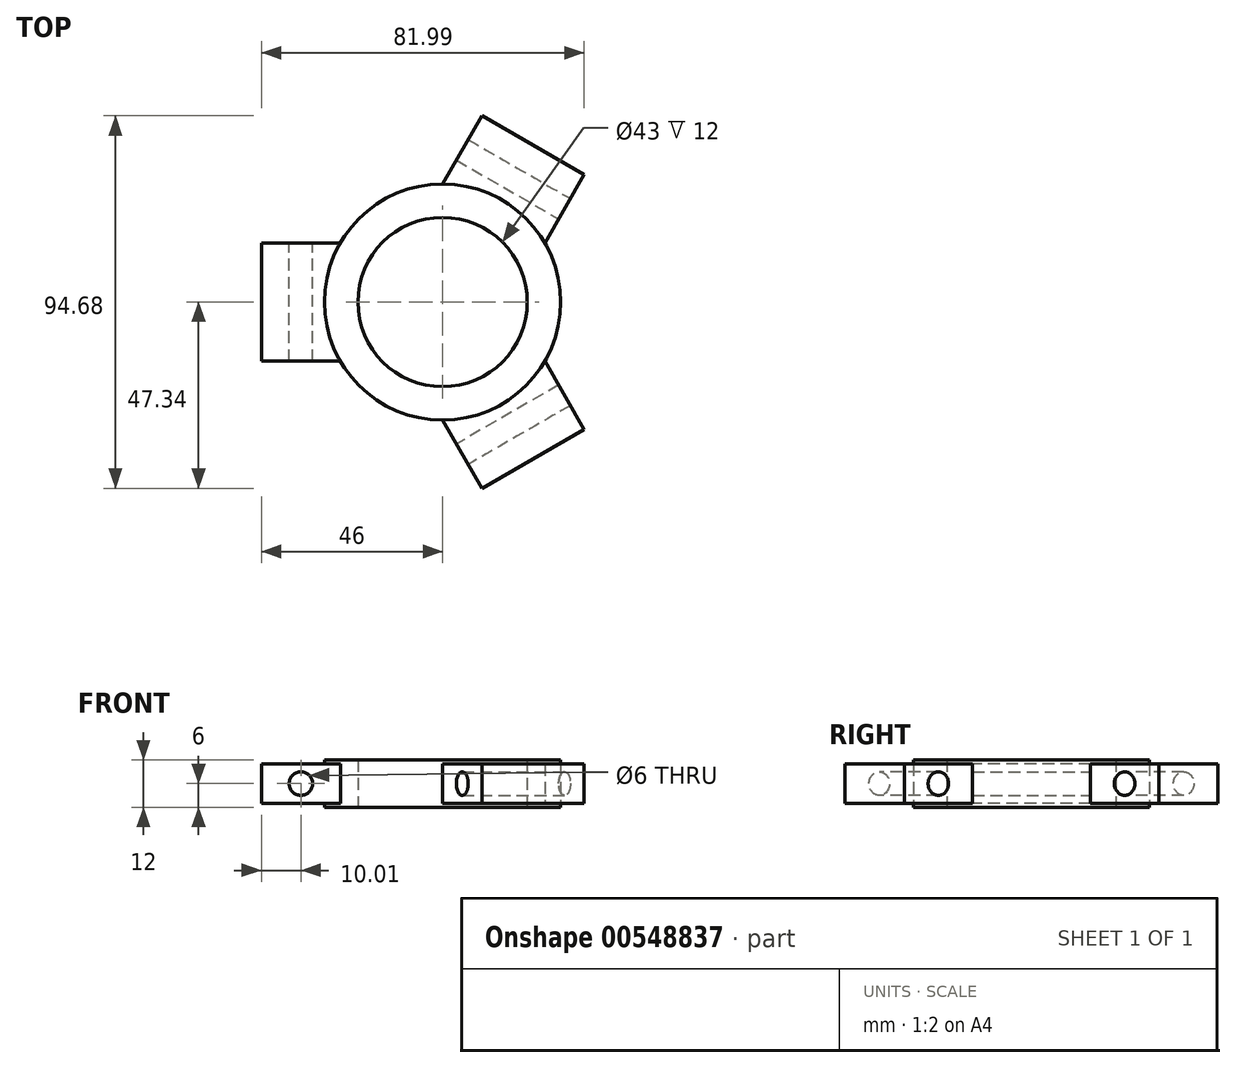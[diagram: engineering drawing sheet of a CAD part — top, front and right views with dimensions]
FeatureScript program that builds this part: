
annotation { "Feature Type Name" : "Feature", "Feature Type Description" : "" }
export const myFeature = defineFeature(function(context is Context, id is Id, definition is map)
    precondition{}
    {
        {
            var Q0;
            Q0=qCreatedBy(makeId("Top.planeOp"),FACE);
            var sketch = newSketch(context, id + "F0", { "sketchPlane" : qUnion([Q0])});
            skLineSegment(sketch, "E0", {"start": v(0, 0) * mm, "end": v(-46, 0) * mm, "construction": true});
            skLineSegment(sketch, "E1", {"start": v(0, 0) * mm, "end": v(23, 39.84) * mm, "construction": true});
            skLineSegment(sketch, "E2", {"start": v(0, 0) * mm, "end": v(23, -39.84) * mm, "construction": true});
            skLineSegment(sketch, "E3", {"start": v(-25.98, 15) * mm, "end": v(-46, 15) * mm});
            skLineSegment(sketch, "E4", {"start": v(-46, 15) * mm, "end": v(-46, -15) * mm});
            skLineSegment(sketch, "E5", {"start": v(-46, -15) * mm, "end": v(-25.98, -15) * mm});
            skLineSegment(sketch, "E6", {"start": v(25.98, -15) * mm, "end": v(36, -32.34) * mm});
            skLineSegment(sketch, "E7", {"start": v(36, -32.34) * mm, "end": v(10, -47.34) * mm});
            skLineSegment(sketch, "E8", {"start": v(10, -47.34) * mm, "end": v(0, -30) * mm});
            skLineSegment(sketch, "E9", {"start": v(0, 30) * mm, "end": v(10, 47.34) * mm});
            skLineSegment(sketch, "E10", {"start": v(10, 47.34) * mm, "end": v(36, 32.34) * mm});
            skLineSegment(sketch, "E11", {"start": v(36, 32.34) * mm, "end": v(25.98, 15) * mm});
            skCircle(sketch, "E12", {"center": v(0, 0) * mm, "radius": 21.5 * mm});
            skCircle(sketch, "E13", {"center": v(0, 0) * mm, "radius": 30 * mm});
            skSolve(sketch);
        }
        {
            var Q0;
            Q0=makeQuery(id+"F0.imprint","IMPRINT",FACE,{"disambiguationData":[TD([[makeQuery(id+"F0.imprint","IMPRINT",EDGE,{"derivedFrom":sQuery(id+"F0.wireOp",EDGE,"E12")}),-1.0]])]});
            extrude(context, id + "F1", {"entities" : qUnion([Q0]), "endBound" : BoundingType.SYMMETRIC, "depth" : 12 * mm, "offsetDistance" : 25 * mm});
        }
        {
            var Q0;
            {var subQ0=sQuery(id+"F0.wireOp",EDGE,"E3");Q0=makeQuery(id+"F0.imprint","IMPRINT",FACE,{"disambiguationData":[TD([[makeQuery(id+"F0.imprint","IMPRINT",EDGE,{"derivedFrom":subQ0}),1.0]])]});}
            var Q1;
            {var subQ0=sQuery(id+"F0.wireOp",EDGE,"E6");Q1=makeQuery(id+"F0.imprint","IMPRINT",FACE,{"disambiguationData":[TD([[makeQuery(id+"F0.imprint","IMPRINT",EDGE,{"derivedFrom":subQ0}),-1.0]])]});}
            var Q2;
            {var subQ0=sQuery(id+"F0.wireOp",EDGE,"E9");Q2=makeQuery(id+"F0.imprint","IMPRINT",FACE,{"disambiguationData":[TD([[makeQuery(id+"F0.imprint","IMPRINT",EDGE,{"derivedFrom":subQ0}),-1.0]])]});}
            extrude(context, id + "F2", {"entities" : qUnion([Q0, Q1, Q2]), "operationType" : NewBodyOperationType.ADD, "endBound" : BoundingType.SYMMETRIC, "depth" : 10 * mm, "offsetDistance" : 25 * mm});
        }
        {
            var Q0;
            Q0=makeQuery(id+"F2.opExtrude","SWEPT_FACE",FACE,{"disambiguationData":[OSD([sQuery(id+"F0.wireOp",EDGE,"E3")])]});
            var sketch = newSketch(context, id + "F3", { "sketchPlane" : qUnion([Q0])});
            skCircle(sketch, "E14", {"center": v(36, 0) * mm, "radius": 3 * mm});
            skPoint(sketch, "E14.centerSnap0", {"position": v(36, -5) * mm});
            skPoint(sketch, "E14.centerSnap1", {"position": v(46, 0) * mm});
            skSolve(sketch);
        }
        {
            var Q0;
            Q0=makeQuery(id+"F2.opExtrude","SWEPT_FACE",FACE,{"disambiguationData":[OSD([sQuery(id+"F0.wireOp",EDGE,"E11")])]});
            var sketch = newSketch(context, id + "F4", { "sketchPlane" : qUnion([Q0])});
            skCircle(sketch, "E15", {"center": v(36, 0) * mm, "radius": 3 * mm});
            skPoint(sketch, "E15.centerSnap0", {"position": v(36, -5) * mm});
            skPoint(sketch, "E15.centerSnap1", {"position": v(46, 0) * mm});
            skSolve(sketch);
        }
        {
            var Q0;
            Q0=makeQuery(id+"F2.opExtrude","SWEPT_FACE",FACE,{"disambiguationData":[OSD([sQuery(id+"F0.wireOp",EDGE,"E8")])]});
            var sketch = newSketch(context, id + "F5", { "sketchPlane" : qUnion([Q0])});
            skCircle(sketch, "E16", {"center": v(36, 0) * mm, "radius": 3 * mm});
            skPoint(sketch, "E16.centerSnap0", {"position": v(46, 0) * mm});
            skPoint(sketch, "E16.centerSnap1", {"position": v(36, -5) * mm});
            skSolve(sketch);
        }
        {
            var Q0;
            Q0 = qSketchRegion(id + "F3", true);
            extrude(context, id + "F6", {"entities" : qUnion([Q0]), "operationType" : NewBodyOperationType.REMOVE, "endBound" : BoundingType.THROUGH_ALL, "oppositeDirection" : true, "depth" : 25 * mm, "offsetDistance" : 25 * mm});
        }
        {
            var Q0;
            Q0 = qSketchRegion(id + "F4", true);
            extrude(context, id + "F7", {"entities" : qUnion([Q0]), "operationType" : NewBodyOperationType.REMOVE, "endBound" : BoundingType.THROUGH_ALL, "oppositeDirection" : true, "depth" : 25 * mm, "offsetDistance" : 25 * mm});
        }
        {
            var Q0;
            Q0 = qSketchRegion(id + "F5", true);
            extrude(context, id + "F8", {"entities" : qUnion([Q0]), "operationType" : NewBodyOperationType.REMOVE, "endBound" : BoundingType.THROUGH_ALL, "oppositeDirection" : true, "depth" : 25 * mm, "offsetDistance" : 25 * mm});
        }
    });
